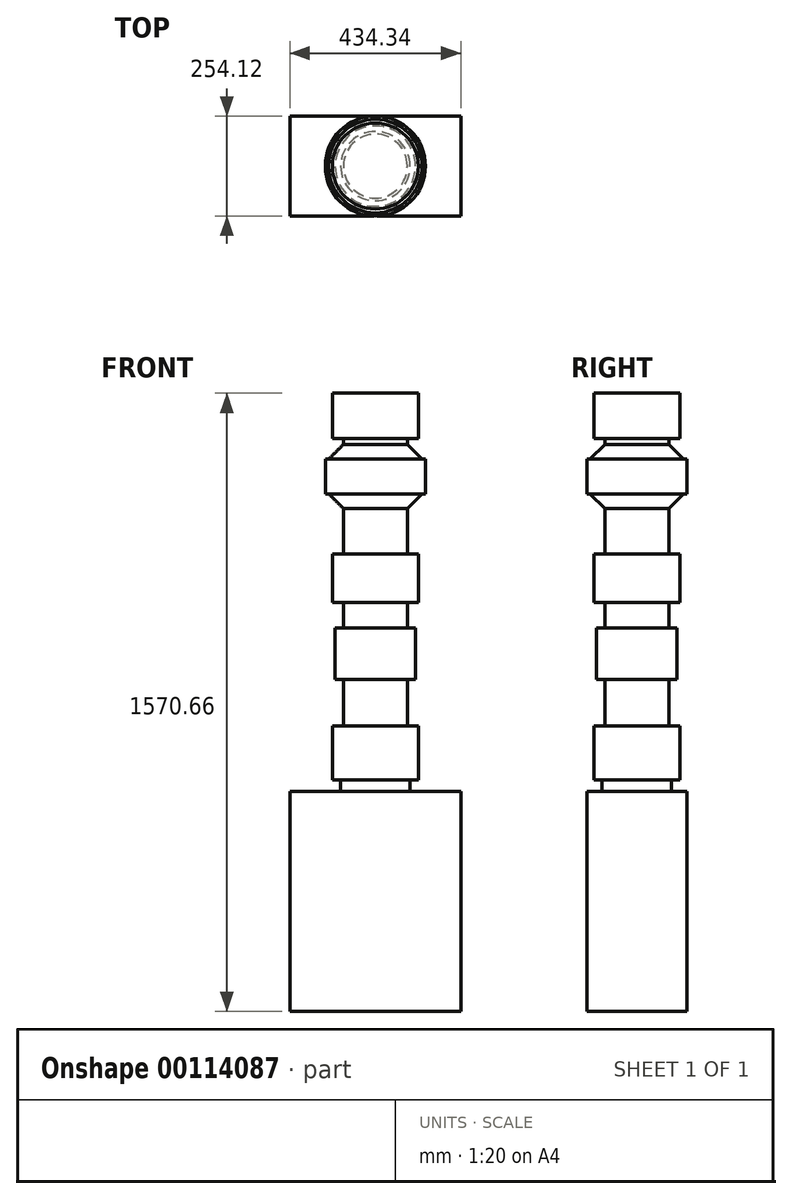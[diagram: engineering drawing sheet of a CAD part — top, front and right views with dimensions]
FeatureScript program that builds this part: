
annotation { "Feature Type Name" : "Feature", "Feature Type Description" : "" }
export const myFeature = defineFeature(function(context is Context, id is Id, definition is map)
    precondition{}
    {
        {
            var Q0;
            Q0=qCreatedBy(makeId("Top.planeOp"),FACE);
            var sketch = newSketch(context, id + "F0", { "sketchPlane" : qUnion([Q0])});
            skLineSegment(sketch, "E0.bottom", {"start": v(-217.17, 127) * mm, "end": v(217.17, 127) * mm});
            skLineSegment(sketch, "E0.top", {"start": v(-217.17, -127) * mm, "end": v(217.17, -127) * mm});
            skLineSegment(sketch, "E0.left", {"start": v(-217.17, 127) * mm, "end": v(-217.17, -127) * mm});
            skLineSegment(sketch, "E0.right", {"start": v(217.17, 127) * mm, "end": v(217.17, -127) * mm});
            skPoint(sketch, "E0.middle", {"position": v(0, 0) * mm});
            skSolve(sketch);
        }
        {
            var Q0;
            Q0 = qSketchRegion(id + "F0", true);
            var Q1;
            Q1=makeQuery(id+"F0.imprint","IMPRINT",FACE,{"disambiguationData":[TD([[makeQuery(id+"F0.imprint","IMPRINT",EDGE,{"derivedFrom":sQuery(id+"F0.wireOp",EDGE,"E0.bottom")}),-1.0]])]});
            extrude(context, id + "F1", {"entities" : qUnion([Q0, Q1]), "depth" : 558.8 * mm});
        }
        {
            var Q0;
            Q0=makeQuery(id+"F1.opExtrude","CAP_FACE",FACE,{"disambiguationData":[OSD([sQuery(id+"F0.wireOp",EDGE,"E0.bottom"),sQuery(id+"F0.wireOp",EDGE,"E0.top"),sQuery(id+"F0.wireOp",EDGE,"E0.left"),sQuery(id+"F0.wireOp",EDGE,"E0.right")])],"isStart":false});
            var sketch = newSketch(context, id + "F2", { "sketchPlane" : qUnion([Q0])});
            skCircle(sketch, "E1", {"center": v(0, 0) * mm, "radius": 88.14 * mm});
            skSolve(sketch);
        }
        {
            var Q0;
            Q0=makeQuery(id+"F2.imprint","IMPRINT",FACE,{"disambiguationData":[TD([[makeQuery(id+"F2.imprint","IMPRINT",EDGE,{"derivedFrom":sQuery(id+"F2.wireOp",EDGE,"E1")}),1.0]])]});
            extrude(context, id + "F3", {"entities" : qUnion([Q0]), "operationType" : NewBodyOperationType.ADD, "depth" : 76.2 * mm});
        }
        {
            var Q0;
            Q0=qCreatedBy(makeId("Front.planeOp"),FACE);
            var sketch = newSketch(context, id + "F4", { "sketchPlane" : qUnion([Q0])});
            skLineSegment(sketch, "E2", {"start": v(0, 588.43) * mm, "end": v(0, 725.38) * mm});
            skLineSegment(sketch, "E3", {"start": v(-81.24, 725.38) * mm, "end": v(-109.1, 725.38) * mm});
            skLineSegment(sketch, "E4", {"start": v(-109.1, 725.38) * mm, "end": v(-109.1, 588.43) * mm});
            skLineSegment(sketch, "E5", {"start": v(-109.1, 588.43) * mm, "end": v(0, 588.43) * mm});
            skLineSegment(sketch, "E6", {"start": v(-81.24, 725.38) * mm, "end": v(-81.24, 843.77) * mm});
            skLineSegment(sketch, "E7", {"start": v(0, 843.77) * mm, "end": v(0, 725.38) * mm});
            skLineSegment(sketch, "E8", {"start": v(-81.24, 973.76) * mm, "end": v(-102.13, 973.76) * mm});
            skLineSegment(sketch, "E9", {"start": v(-102.13, 973.76) * mm, "end": v(-102.13, 843.77) * mm});
            skLineSegment(sketch, "E10", {"start": v(-102.13, 843.77) * mm, "end": v(-81.24, 843.77) * mm});
            skLineSegment(sketch, "E11", {"start": v(-81.24, 973.76) * mm, "end": v(-81.24, 1038.75) * mm});
            skLineSegment(sketch, "E12", {"start": v(0, 1038.75) * mm, "end": v(0, 843.77) * mm});
            skLineSegment(sketch, "E13", {"start": v(-109.1, 1038.75) * mm, "end": v(-81.24, 1038.75) * mm});
            skLineSegment(sketch, "E14", {"start": v(-109.1, 1038.75) * mm, "end": v(-109.1, 1161.78) * mm});
            skLineSegment(sketch, "E15", {"start": v(-109.1, 1161.78) * mm, "end": v(-81.24, 1161.78) * mm});
            skLineSegment(sketch, "E16", {"start": v(0, 1161.78) * mm, "end": v(0, 1038.75) * mm});
            skLineSegment(sketch, "E17", {"start": v(-81.24, 1161.78) * mm, "end": v(-81.24, 1277.84) * mm});
            skLineSegment(sketch, "E18", {"start": v(-81.24, 1277.84) * mm, "end": v(-118.38, 1314.98) * mm});
            skLineSegment(sketch, "E19", {"start": v(-118.38, 1314.98) * mm, "end": v(-127.06, 1314.98) * mm});
            skLineSegment(sketch, "E20", {"start": v(-127.06, 1314.98) * mm, "end": v(-127.06, 1403) * mm});
            skLineSegment(sketch, "E21", {"start": v(-127.06, 1403) * mm, "end": v(-118.77, 1403) * mm});
            skLineSegment(sketch, "E22", {"start": v(-118.77, 1403) * mm, "end": v(-81.24, 1440.53) * mm});
            skLineSegment(sketch, "E23", {"start": v(-81.24, 1440.53) * mm, "end": v(-81.24, 1455.51) * mm});
            skLineSegment(sketch, "E24", {"start": v(-81.24, 1455.51) * mm, "end": v(-109.1, 1455.51) * mm});
            skLineSegment(sketch, "E25", {"start": v(-109.1, 1455.51) * mm, "end": v(-109.1, 1570.66) * mm});
            skLineSegment(sketch, "E26", {"start": v(-109.1, 1570.66) * mm, "end": v(0, 1570.66) * mm});
            skLineSegment(sketch, "E27", {"start": v(0, 1570.66) * mm, "end": v(0, 1161.78) * mm});
            skPoint(sketch, "E28.orphan", {"position": v(0, 973.76) * mm});
            skLineSegment(sketch, "E29", {"start": v(0, 1570.66) * mm, "end": v(0, 1700.26) * mm, "construction": true});
            skSolve(sketch);
        }
        {
            var Q0;
            Q0 = qSketchRegion(id + "F4", true);
            var Q1;
            Q1=makeQuery(id+"F4.imprint","IMPRINT",FACE,{"disambiguationData":[TD([[makeQuery(id+"F4.imprint","IMPRINT",EDGE,{"derivedFrom":sQuery(id+"F4.wireOp",EDGE,"E2")}),1.0]])]});
            var Q2;
            Q2=sQuery(id+"F4.wireOp",EDGE,"E29");
            revolve(context, id + "F5", {"operationType" : NewBodyOperationType.ADD, "entities" : qUnion([Q0, Q1]), "axis" : qUnion([Q2]), "revolveType" : RevolveType.FULL});
        }
    });
